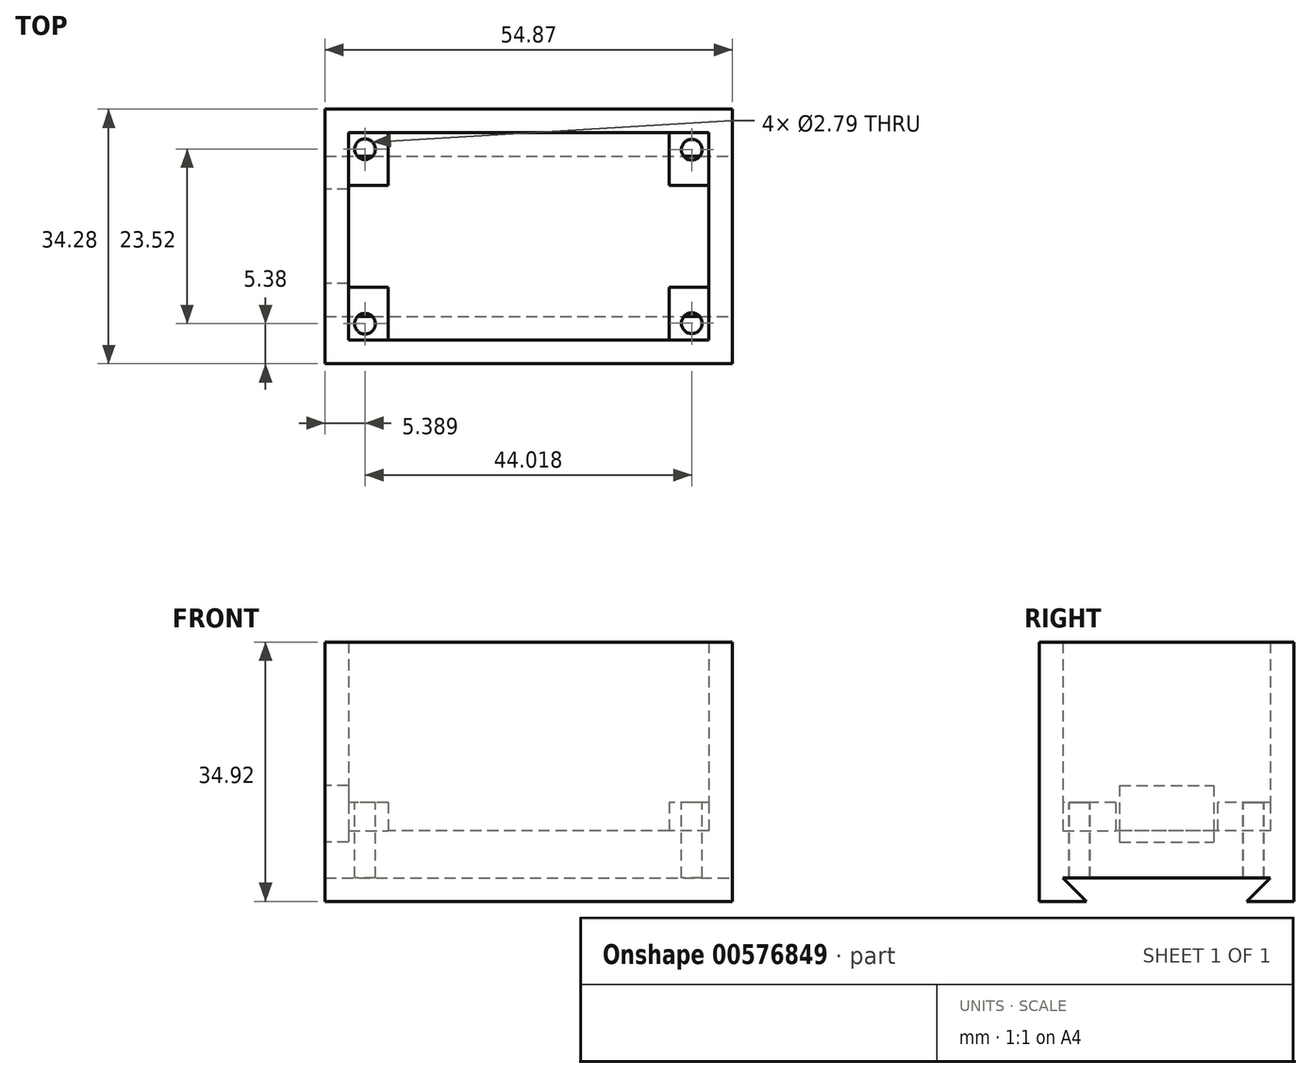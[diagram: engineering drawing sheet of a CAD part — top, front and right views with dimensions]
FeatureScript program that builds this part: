
annotation { "Feature Type Name" : "Feature", "Feature Type Description" : "" }
export const myFeature = defineFeature(function(context is Context, id is Id, definition is map)
    precondition{}
    {
        {
            var Q0;
            Q0=qCreatedBy(makeId("Top.planeOp"),FACE);
            var sketch = newSketch(context, id + "F0", { "sketchPlane" : qUnion([Q0])});
            skLineSegment(sketch, "E0.bottom", {"start": v(29.14, 17.15) * mm, "end": v(-25.73, 17.14) * mm});
            skLineSegment(sketch, "E0.top", {"start": v(29.14, -17.14) * mm, "end": v(-25.73, -17.15) * mm});
            skLineSegment(sketch, "E0.left", {"start": v(29.14, 17.15) * mm, "end": v(29.14, -17.14) * mm});
            skLineSegment(sketch, "E0.right", {"start": v(-25.73, 17.14) * mm, "end": v(-25.73, -17.15) * mm});
            skPoint(sketch, "E0.middle", {"position": v(1.7, 0) * mm});
            skSolve(sketch);
        }
        {
            var Q0;
            Q0 = qSketchRegion(id + "F0", true);
            extrude(context, id + "F1", {"entities" : qUnion([Q0]), "depth" : 28.57 * mm, "offsetDistance" : 25.4 * mm});
        }
        {
            var Q0;
            Q0=makeQuery(id+"F1.opExtrude","CAP_FACE",FACE,{"disambiguationData":[OSD([sQuery(id+"F0.wireOp",EDGE,"E0.bottom"),sQuery(id+"F0.wireOp",EDGE,"E0.top"),sQuery(id+"F0.wireOp",EDGE,"E0.left"),sQuery(id+"F0.wireOp",EDGE,"E0.right")])],"isStart":false});
            shell(context, id + "F2", {"entities" : qUnion([Q0]), "thickness" : 3.17 * mm});
        }
        {
            var Q0;
            Q0=makeQuery(id+"F2.opShell","OFFSET_FACE",FACE,{"disambiguationData":[OSD([sQuery(id+"F0.wireOp",EDGE,"E0.bottom"),sQuery(id+"F0.wireOp",EDGE,"E0.top"),sQuery(id+"F0.wireOp",EDGE,"E0.left"),sQuery(id+"F0.wireOp",EDGE,"E0.right")])]});
            var sketch = newSketch(context, id + "F3", { "sketchPlane" : qUnion([Q0])});
            skLineSegment(sketch, "E1.bottom", {"start": v(-22.55, 13.97) * mm, "end": v(-17.22, 13.97) * mm});
            skLineSegment(sketch, "E1.top", {"start": v(-22.55, 6.86) * mm, "end": v(-17.22, 6.86) * mm});
            skLineSegment(sketch, "E1.left", {"start": v(-22.55, 13.97) * mm, "end": v(-22.55, 6.86) * mm});
            skLineSegment(sketch, "E1.right", {"start": v(-17.22, 13.97) * mm, "end": v(-17.22, 6.86) * mm});
            skLineSegment(sketch, "E2.bottom", {"start": v(-22.55, -13.97) * mm, "end": v(-17.22, -13.97) * mm});
            skLineSegment(sketch, "E2.top", {"start": v(-22.55, -6.86) * mm, "end": v(-17.22, -6.86) * mm});
            skLineSegment(sketch, "E2.left", {"start": v(-22.55, -13.97) * mm, "end": v(-22.55, -6.86) * mm});
            skLineSegment(sketch, "E2.right", {"start": v(-17.22, -13.97) * mm, "end": v(-17.22, -6.86) * mm});
            skLineSegment(sketch, "E3.bottom", {"start": v(25.96, -13.97) * mm, "end": v(20.63, -13.97) * mm});
            skLineSegment(sketch, "E3.top", {"start": v(25.96, -6.86) * mm, "end": v(20.63, -6.86) * mm});
            skLineSegment(sketch, "E3.left", {"start": v(25.96, -13.97) * mm, "end": v(25.96, -6.86) * mm});
            skLineSegment(sketch, "E3.right", {"start": v(20.63, -13.97) * mm, "end": v(20.63, -6.86) * mm});
            skLineSegment(sketch, "E4.bottom", {"start": v(25.96, 13.97) * mm, "end": v(20.63, 13.97) * mm});
            skLineSegment(sketch, "E4.top", {"start": v(25.96, 6.86) * mm, "end": v(20.63, 6.86) * mm});
            skLineSegment(sketch, "E4.left", {"start": v(25.96, 13.97) * mm, "end": v(25.96, 6.86) * mm});
            skLineSegment(sketch, "E4.right", {"start": v(20.63, 13.97) * mm, "end": v(20.63, 6.86) * mm});
            skSolve(sketch);
        }
        {
            var Q0;
            Q0 = qSketchRegion(id + "F3", true);
            extrude(context, id + "F4", {"entities" : qUnion([Q0]), "operationType" : NewBodyOperationType.ADD, "depth" : 3.8 * mm, "offsetDistance" : 25.4 * mm});
        }
        {
            var Q0;
            Q0=makeQuery(id+"F1.opExtrude","SWEPT_FACE",FACE,{"disambiguationData":[OSD([sQuery(id+"F0.wireOp",EDGE,"E0.left")])]});
            var sketch = newSketch(context, id + "F5", { "sketchPlane" : qUnion([Q0])});
            skLineSegment(sketch, "E5.bottom", {"start": v(17.15, 0) * mm, "end": v(-17.15, 0) * mm});
            skLineSegment(sketch, "E5.top", {"start": v(17.15, -6.35) * mm, "end": v(10.8, -6.35) * mm});
            skLineSegment(sketch, "E5.left", {"start": v(17.15, 0) * mm, "end": v(17.15, -6.35) * mm});
            skLineSegment(sketch, "E5.right", {"start": v(-17.15, 0) * mm, "end": v(-17.15, -6.35) * mm});
            skLineSegment(sketch, "E6", {"start": v(13.97, -3.17) * mm, "end": v(-13.97, -3.18) * mm});
            skLineSegment(sketch, "E7", {"start": v(-10.8, -3.72) * mm, "end": v(-10.8, -3.18) * mm});
            skPoint(sketch, "E7.startSnap0", {"position": v(-10.8, -3.72) * mm});
            skLineSegment(sketch, "E8", {"start": v(-13.97, -3.18) * mm, "end": v(-10.8, -6.35) * mm});
            skLineSegment(sketch, "E9.MirrorCS", {"start": v(13.97, -3.18) * mm, "end": v(10.8, -6.35) * mm});
            skPoint(sketch, "E10.orphan", {"position": v(17.15, -3.17) * mm});
            skPoint(sketch, "E11.orphan", {"position": v(-13.97, -6.35) * mm});
            skPoint(sketch, "E12.orphan", {"position": v(-17.15, -3.18) * mm});
            skPoint(sketch, "E13.end.orphan", {"position": v(-13.97, 0) * mm});
            skLineSegment(sketch, "E14.trimOffspring", {"start": v(-10.8, -6.35) * mm, "end": v(-17.15, -6.35) * mm});
            skSolve(sketch);
        }
        {
            var Q0;
            Q0 = qSketchRegion(id + "F5", true);
            extrude(context, id + "F6", {"entities" : qUnion([Q0]), "operationType" : NewBodyOperationType.ADD, "oppositeDirection" : true, "depth" : 54.86 * mm, "offsetDistance" : 25.4 * mm});
        }
        {
            var Q0;
            Q0=makeQuery(id+"F4.opExtrude","CAP_FACE",FACE,{"disambiguationData":[OSD([sQuery(id+"F3.wireOp",EDGE,"E4.bottom"),sQuery(id+"F3.wireOp",EDGE,"E4.top"),sQuery(id+"F3.wireOp",EDGE,"E4.left"),sQuery(id+"F3.wireOp",EDGE,"E4.right")])],"isStart":false});
            var sketch = newSketch(context, id + "F7", { "sketchPlane" : qUnion([Q0])});
            skCircle(sketch, "E15", {"center": v(-20.34, 11.76) * mm, "radius": 1.4 * mm});
            skPoint(sketch, "E15.first.point", {"position": v(-21.4, 12.68) * mm});
            skPoint(sketch, "E15.second.point", {"position": v(-19.32, 10.8) * mm});
            skPoint(sketch, "E15.third.point", {"position": v(-21.15, 10.62) * mm});
            skCircle(sketch, "E16.MirrorC", {"center": v(-20.34, -11.76) * mm, "radius": 1.4 * mm});
            skCircle(sketch, "E17", {"center": v(23.68, 11.68) * mm, "radius": 1.4 * mm});
            skPoint(sketch, "E17.first.point", {"position": v(22.77, 12.75) * mm});
            skPoint(sketch, "E17.second.point", {"position": v(24.26, 10.41) * mm});
            skPoint(sketch, "E17.second.point.positionSnap0", {"position": v(20.63, 10.41) * mm});
            skPoint(sketch, "E17.third.point", {"position": v(23.37, 10.32) * mm});
            skCircle(sketch, "E18.MirrorC", {"center": v(23.68, -11.68) * mm, "radius": 1.4 * mm});
            skSolve(sketch);
        }
        {
            var Q0;
            Q0=sQuery(id+"F7.wireOp",VERTEX,"E15.center");
            var Q1;
            Q1=sQuery(id+"F7.wireOp",VERTEX,"E17.center");
            var Q2;
            Q2=sQuery(id+"F7.wireOp",VERTEX,"E18.MirrorC.center");
            var Q3;
            Q3=sQuery(id+"F7.wireOp",VERTEX,"E16.MirrorC.center");
            var Q4;
            Q4=makeQuery(id+"F1.opExtrude","SWEPT_BODY",BODY,{"disambiguationData":[OSD([sQuery(id+"F0.wireOp",EDGE,"E0.bottom"),sQuery(id+"F0.wireOp",EDGE,"E0.top"),sQuery(id+"F0.wireOp",EDGE,"E0.left"),sQuery(id+"F0.wireOp",EDGE,"E0.right")])]});
            hole(context, id + "F8", {"style" : HoleStyle.SIMPLE, "endStyle" : HoleEndStyle.BLIND, "holeDiameter" : 2.8 * mm, "holeDepth" : 10.16 * mm, "isTappedThrough" : true, "tappedDepth" : 12.7 * mm, "tapClearance" : 3, "locations" : qUnion([Q0, Q1, Q2, Q3]), "scope" : qUnion([Q4])});
        }
        {
            var Q0;
            Q0=makeQuery(id+"F6.boolean.opBoolean","MERGE",FACE,{"derivedFrom":[makeQuery(id+"F1.opExtrude","SWEPT_FACE",FACE,{"disambiguationData":[OSD([sQuery(id+"F0.wireOp",EDGE,"E0.right")])]}),makeQuery(id+"F6.opExtrude","CAP_FACE",FACE,{"disambiguationData":[OSD([sQuery(id+"F5.wireOp",EDGE,"E5.bottom"),sQuery(id+"F5.wireOp",EDGE,"E5.top"),sQuery(id+"F5.wireOp",EDGE,"E5.left"),sQuery(id+"F5.wireOp",EDGE,"E5.right"),sQuery(id+"F5.wireOp",EDGE,"E6"),sQuery(id+"F5.wireOp",EDGE,"E8"),sQuery(id+"F5.wireOp",EDGE,"E9.MirrorCS"),sQuery(id+"F5.wireOp",EDGE,"E14.trimOffspring")])],"isStart":false})]});
            var sketch = newSketch(context, id + "F9", { "sketchPlane" : qUnion([Q0])});
            skLineSegment(sketch, "E19.bottom", {"start": v(6.35, 9.27) * mm, "end": v(-6.35, 9.27) * mm});
            skLineSegment(sketch, "E19.top", {"start": v(6.35, 1.65) * mm, "end": v(-6.35, 1.65) * mm});
            skLineSegment(sketch, "E19.left", {"start": v(6.35, 9.27) * mm, "end": v(6.35, 1.65) * mm});
            skLineSegment(sketch, "E19.right", {"start": v(-6.35, 9.27) * mm, "end": v(-6.35, 1.65) * mm});
            skPoint(sketch, "E19.middle", {"position": v(0, 5.46) * mm});
            skSolve(sketch);
        }
        {
            var Q0;
            Q0 = qSketchRegion(id + "F9", true);
            extrude(context, id + "F10", {"entities" : qUnion([Q0]), "operationType" : NewBodyOperationType.REMOVE, "oppositeDirection" : true, "depth" : 3.17 * mm, "offsetDistance" : 25.4 * mm});
        }
    });
